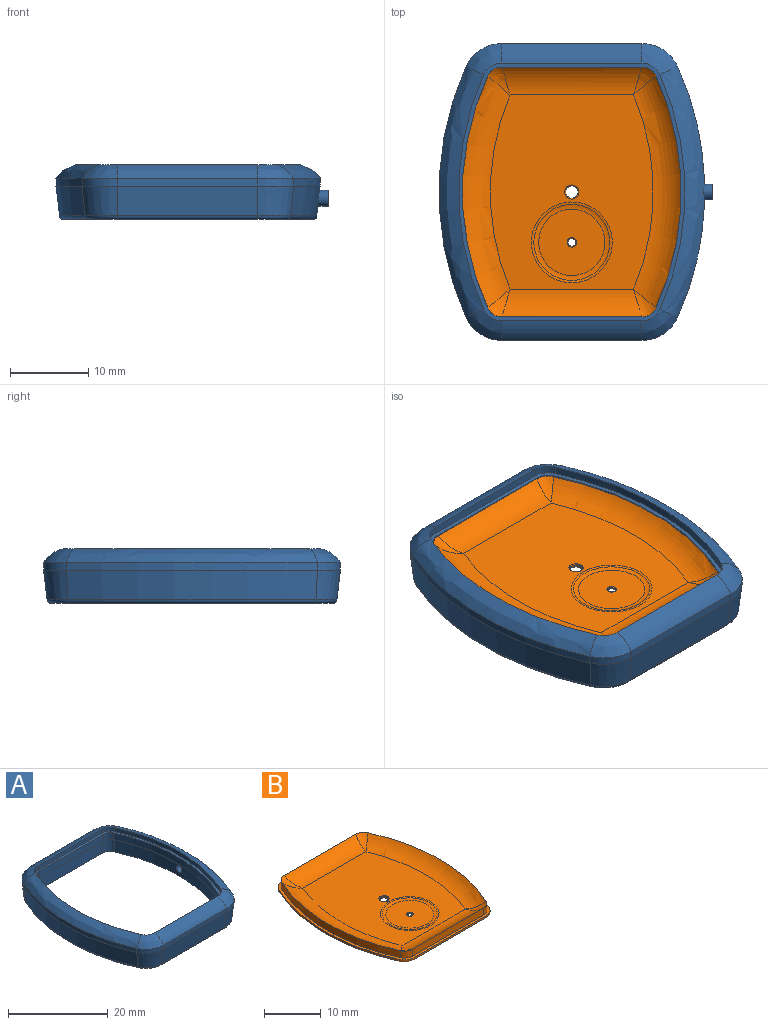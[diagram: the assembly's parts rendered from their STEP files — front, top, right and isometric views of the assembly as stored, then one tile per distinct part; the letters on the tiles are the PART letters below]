
ASSEMBLY  parts=2 mates=1
PART A: 75 faces, bbox 39.5x38x7 mm
  f0: cone r=39mm half-angle=6.7deg, axis (0,0,1), area 53.6mm2, adj f3,f5,f25,f74
  f1: cone r=39mm half-angle=6.7deg, axis (0,0,1), area 53.6mm2, adj f2,f5,f36,f74
  f2: cylinder r=39mm len=15.03mm, axis (0,0,1), area 14.8mm2, adj f1,f4,f37,f74
  f3: cylinder r=39mm len=15.03mm, axis (0,0,1), area 14.8mm2, adj f0,f4,f26,f74
  f4: bspline ~32.12x6.96mm, area 100.2mm2, adj f2,f3,f20,f27,f31,f74
  f5: torus R=38.06mm, axis (0,0,-1), area 23.2mm2, adj f0,f1,f60,f64,f67,f71,f74
  f6: bspline ~4.56x3.97mm, area 13.9mm2, adj f7,f12,f13,f52
  f7: cylinder r=2.5mm len=2.28mm, axis (0,0,1), area 2.9mm2, adj f6,f14,f53,f54
  f8: cylinder r=2mm len=1.82mm, axis (0,0,1), area 3.8mm2, adj f15,f54,f55,f56
  f9: cylinder r=2.5mm len=3.35mm, axis (0,0,1), area 9.6mm2, adj f16,f56,f57,f58
  f10: cylinder r=4mm len=3.65mm, axis (0,0,1), area 4.6mm2, adj f17,f58,f59,f60
  f11: cone r=5mm half-angle=6.7deg, axis (0,0,1), area 21mm2, adj f12,f18,f61,f68
  f12: cylinder r=5mm len=4.56mm, axis (0,0,1), area 5.7mm2, adj f6,f11,f19,f62
  f13: bspline ~17.97x2.5mm, area 56.2mm2, adj f6,f14,f19,f20
  f14: plane 17.97x1mm, normal (0,-1,0), area 18mm2, adj f7,f13,f21,f54
  f15: plane 17.97x1.65mm, normal (0,-1,0), area 29.6mm2, adj f8,f22,f54,f56
  f16: plane 17.97x3.35mm, normal (0,-1,0), area 60.2mm2, adj f9,f23,f56,f58
  f17: plane 17.97x1mm, normal (0,-1,0), area 18mm2, adj f10,f24,f58,f60
  f18: plane 17.97x3.81mm, normal (0,0.99,-0.12), area 68.9mm2, adj f11,f19,f25,f69
  f19: plane 17.97x1mm, normal (0,1,0), area 18mm2, adj f12,f13,f18,f26
  f20: bspline ~4.56x3.97mm, area 13.9mm2, adj f4,f13,f21,f26
  f21: cylinder r=2.5mm len=2.28mm, axis (0,0,1), area 2.9mm2, adj f14,f20,f27,f54
  f22: cylinder r=2mm len=1.82mm, axis (0,0,1), area 3.8mm2, adj f15,f28,f54,f56
  f23: cylinder r=2.5mm len=3.35mm, axis (0,0,1), area 9.6mm2, adj f16,f29,f56,f58
  f24: cylinder r=4mm len=3.65mm, axis (0,0,1), area 4.6mm2, adj f17,f30,f58,f60
  f25: cone r=5mm half-angle=6.7deg, axis (0,0,1), area 21mm2, adj f0,f18,f26,f67
  f26: cylinder r=5mm len=4.56mm, axis (0,0,1), area 5.7mm2, adj f3,f19,f20,f25
  f27: cylinder r=36.5mm len=30.06mm, axis (0,0,1), area 31mm2, adj f4,f21,f32,f54
  f28: cylinder r=36mm len=29.65mm, axis (0,0,1), area 50.4mm2, adj f22,f33,f54,f56
  f29: cylinder r=36.5mm len=30.06mm, axis (0,0,1), area 102mm2, adj f23,f34,f56,f58,f72
  f30: cylinder r=38mm len=31.29mm, axis (0,0,1), area 32.3mm2, adj f24,f35,f58,f60
  f31: bspline ~4.56x3.97mm, area 13.9mm2, adj f4,f32,f37,f38
  f32: cylinder r=2.5mm len=2.28mm, axis (0,0,1), area 2.9mm2, adj f27,f31,f39,f54
  f33: cylinder r=2mm len=1.82mm, axis (0,0,1), area 3.8mm2, adj f28,f40,f54,f56
  f34: cylinder r=2.5mm len=3.35mm, axis (0,0,1), area 9.6mm2, adj f29,f41,f56,f58
  f35: cylinder r=4mm len=3.65mm, axis (0,0,1), area 4.6mm2, adj f30,f42,f58,f60
  f36: cone r=5mm half-angle=6.7deg, axis (0,0,1), area 21mm2, adj f1,f37,f43,f64
  f37: cylinder r=5mm len=4.56mm, axis (0,0,1), area 5.7mm2, adj f2,f31,f36,f44
  f38: bspline ~17.97x2.5mm, area 56.2mm2, adj f31,f39,f44,f45
  f39: plane 17.97x1mm, normal (0,1,0), area 18mm2, adj f32,f38,f46,f54
  f40: plane 17.97x1.65mm, normal (0,1,0), area 29.6mm2, adj f33,f47,f54,f56
  f41: plane 17.97x3.35mm, normal (0,1,0), area 60.2mm2, adj f34,f48,f56,f58
  f42: plane 17.97x1mm, normal (0,1,0), area 18mm2, adj f35,f49,f58,f60
  f43: plane 17.97x3.81mm, normal (0,-0.99,-0.12), area 68.9mm2, adj f36,f44,f50,f63
  f44: plane 17.97x1mm, normal (0,-1,0), area 18mm2, adj f37,f38,f43,f51
  f45: bspline ~4.56x3.97mm, area 13.9mm2, adj f38,f46,f51,f52
  f46: cylinder r=2.5mm len=2.28mm, axis (0,0,1), area 2.9mm2, adj f39,f45,f53,f54
  f47: cylinder r=2mm len=1.82mm, axis (0,0,1), area 3.8mm2, adj f40,f54,f55,f56
  f48: cylinder r=2.5mm len=3.35mm, axis (0,0,1), area 9.6mm2, adj f41,f56,f57,f58
  f49: cylinder r=4mm len=3.65mm, axis (0,0,1), area 4.6mm2, adj f42,f58,f59,f60
  f50: cone r=5mm half-angle=6.7deg, axis (0,0,1), area 21mm2, adj f43,f51,f61,f65
  f51: cylinder r=5mm len=4.56mm, axis (0,0,1), area 5.7mm2, adj f44,f45,f50,f62
  f52: bspline ~32.12x6.96mm, area 100.5mm2, adj f6,f45,f53,f62
  f53: cylinder r=36.5mm len=30.06mm, axis (0,0,1), area 31mm2, adj f7,f46,f52,f54
  f54: plane 33x29mm, normal (0,0,1), area 53.9mm2, adj f7,f8,f14,f15,f21,f22,f27,f28
  f55: cylinder r=36mm len=29.65mm, axis (0,0,1), area 50.4mm2, adj f8,f47,f54,f56
  f56: plane 33x29mm, normal (0,0,-1), area 53.9mm2, adj f8,f9,f15,f16,f22,f23,f28,f29
  f57: cylinder r=36.5mm len=30.06mm, axis (0,0,1), area 103.8mm2, adj f9,f48,f56,f58
  f58: plane 36x32mm, normal (0,0,-1), area 171.1mm2, adj f9,f10,f16,f17,f23,f24,f29,f30
  f59: cylinder r=38mm len=31.29mm, axis (0,0,1), area 32.3mm2, adj f10,f49,f58,f60
  f60: plane 36.11x32.11mm, normal (0,0,-1), area 6.6mm2, adj f5,f10,f17,f24,f30,f35,f42,f49
  f61: cone r=39mm half-angle=6.7deg, axis (0,0,1), area 126.2mm2, adj f11,f50,f62,f66
  f62: cylinder r=39mm len=32.12mm, axis (0,0,1), area 33.1mm2, adj f12,f51,f52,f61
  f63: cylinder r=0.5mm len=17.97mm, axis (1,0,0), area 13.1mm2, adj f43,f60,f64,f65
  f64: torus R=4.06mm, axis (0,0,-1), area 3.6mm2, adj f5,f36,f60,f63
  f65: torus R=4.06mm, axis (0,0,-1), area 3.6mm2, adj f50,f60,f63,f66
  f66: torus R=38.06mm, axis (0,0,-1), area 23.7mm2, adj f60,f61,f65,f68
  f67: torus R=4.06mm, axis (0,0,-1), area 3.6mm2, adj f5,f25,f60,f69
  f68: torus R=4.06mm, axis (0,0,-1), area 3.6mm2, adj f11,f60,f66,f69
  f69: cylinder r=0.5mm len=17.97mm, axis (-1,0,0), area 13.1mm2, adj f18,f60,f67,f68
  f70: cylinder r=1mm len=2mm, axis (1,0,0), area 9.4mm2, adj f71,f73
  f71: plane 5.5x5.18mm, normal (1,0,0), area 20mm2, adj f5,f70,f74
  f72: cylinder r=0.75mm len=3.5mm, axis (1,0,0), area 16.5mm2, adj f29,f73
  f73: plane 2x2mm, normal (1,0,0), area 1.4mm2, adj f70,f72
  f74: cylinder r=2.75mm len=5.5mm, axis (-1,0,0), area 4mm2, adj f0,f1,f2,f3,f4,f5,f71
PART B: 34 faces, bbox 36.9x33.4x5.4 mm
  f0: plane 24.86x20.86mm, normal (0,0,1), area 390.7mm2, adj f22,f23,f26,f27,f30,f33
  f1: plane 8.48x8.48mm, normal (0,0,1), area 55.3mm2, adj f2,f32
  f2: torus R=4.24mm, axis (0,0,-1), area 18.2mm2, adj f1,f33
  f3: cylinder r=2mm len=1.82mm, axis (0,0,1), area 3.4mm2, adj f4,f10,f20,f25
  f4: plane 17.87x1.5mm, normal (0,1,0), area 26.8mm2, adj f3,f5,f20,f27
  f5: cylinder r=2mm len=1.82mm, axis (0,0,1), area 3.4mm2, adj f4,f6,f20,f28
  f6: cylinder r=35.5mm len=29.67mm, axis (0,0,1), area 45.9mm2, adj f5,f7,f20,f26
  f7: cylinder r=2mm len=1.82mm, axis (0,0,1), area 3.4mm2, adj f6,f8,f20,f24
  f8: plane 17.87x1.5mm, normal (0,-1,0), area 26.8mm2, adj f7,f9,f20,f22
  f9: cylinder r=2mm len=1.82mm, axis (0,0,1), area 3.4mm2, adj f8,f10,f20,f21
  f10: cylinder r=35.5mm len=29.67mm, axis (0,0,1), area 45.9mm2, adj f3,f9,f20,f23
  f11: plane 33x29mm, normal (0,0,-1), area 867.7mm2, adj f12,f13,f14,f15,f16,f17,f18,f19
  f12: cylinder r=2.5mm len=2.28mm, axis (0,0,-1), area 1.1mm2, adj f11,f13,f19,f20
  f13: plane 17.97x0.4mm, normal (0,-1,0), area 7.2mm2, adj f11,f12,f14,f20
  f14: cylinder r=2.5mm len=2.28mm, axis (0,0,-1), area 1.1mm2, adj f11,f13,f15,f20
  f15: cylinder r=36.5mm len=30.06mm, axis (0,0,-1), area 12.4mm2, adj f11,f14,f16,f20
  f16: cylinder r=2.5mm len=2.28mm, axis (0,0,-1), area 1.1mm2, adj f11,f15,f17,f20
  f17: plane 17.97x0.4mm, normal (0,1,0), area 7.2mm2, adj f11,f16,f18,f20
  f18: cylinder r=2.5mm len=2.28mm, axis (0,0,-1), area 1.1mm2, adj f11,f17,f19,f20
  f19: cylinder r=36.5mm len=30.06mm, axis (0,0,-1), area 12.4mm2, adj f11,f12,f18,f20
  f20: plane 33x29mm, normal (0,0,1), area 55.1mm2, adj f3,f4,f5,f6,f7,f8,f9,f10
  f21: bspline ~3.57x2.84mm, area 5mm2, adj f9,f22,f23
  f22: cylinder r=5mm len=17.87mm, axis (1,0,0), area 67mm2, adj f0,f8,f21,f24
  f23: torus R=31.93mm, axis (0,0,-1), area 111.8mm2, adj f0,f10,f21,f25
  f24: bspline ~3.57x2.84mm, area 5mm2, adj f7,f22,f26
  f25: bspline ~3.57x2.84mm, area 5mm2, adj f3,f23,f27
  f26: torus R=31.93mm, axis (0,0,-1), area 111.8mm2, adj f0,f6,f24,f28
  f27: cylinder r=5mm len=17.87mm, axis (-1,0,0), area 67mm2, adj f0,f4,f25,f28
  f28: bspline ~3.57x2.84mm, area 5mm2, adj f5,f26,f27
  f29: cylinder r=0.8mm len=1.6mm, axis (0,0,1), area 1.5mm2, adj f11,f30
  f30: torus R=0.9mm, axis (0,0,1), area 0.8mm2, adj f0,f29
  f31: cylinder r=0.5mm len=1mm, axis (0,0,1), area 0.5mm2, adj f11,f32
  f32: torus R=0.6mm, axis (0,0,1), area 0.5mm2, adj f1,f31
  f33: torus R=5.18mm, axis (0,0,1), area 10mm2, adj f0,f2
PLACE A t=(-2.45,10.73,3.49)mm fixed
PLACE B t=(-2.45,10.73,7.44)mm
MATE fastened B.f20 <-> A.f56  axis (0,0,1) through (-11.44,-5.77,7.84)mm
